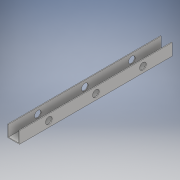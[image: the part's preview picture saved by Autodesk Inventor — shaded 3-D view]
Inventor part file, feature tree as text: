
AUTODESK INVENTOR PART (.ipt)
format: ipt  version: 2018 (Build 220112000, 112)  size: 122,880 bytes
history: native  units: in
note: dims shown in document units (in); Inventor stores cm internally (conversion verified against a paired STEP export)
features: extrude x2, sketch x2
ambient origin geometry x8: Origin, YZ Plane, XZ Plane, XY Plane, X Axis, Y Axis, Z Axis, Center Point
bodies: Solid1 (feature_tree)
feature tree (4):
  extrude  "Extrusion1"  Depth=0.125in
  extrude  "Extrusion2"  Depth=0.125in
  sketch  "Sketch1"  dims[d0=2.0in d1=0.125in]
  sketch  "Sketch2"  dims[d2=2.0in d3=0.125in d4=2.0in d5=0.125in d6=26.0in d7=0.0in d8=5.0in d9=5.0in d10=1.125in d11=2.125in d12=0.0in]
